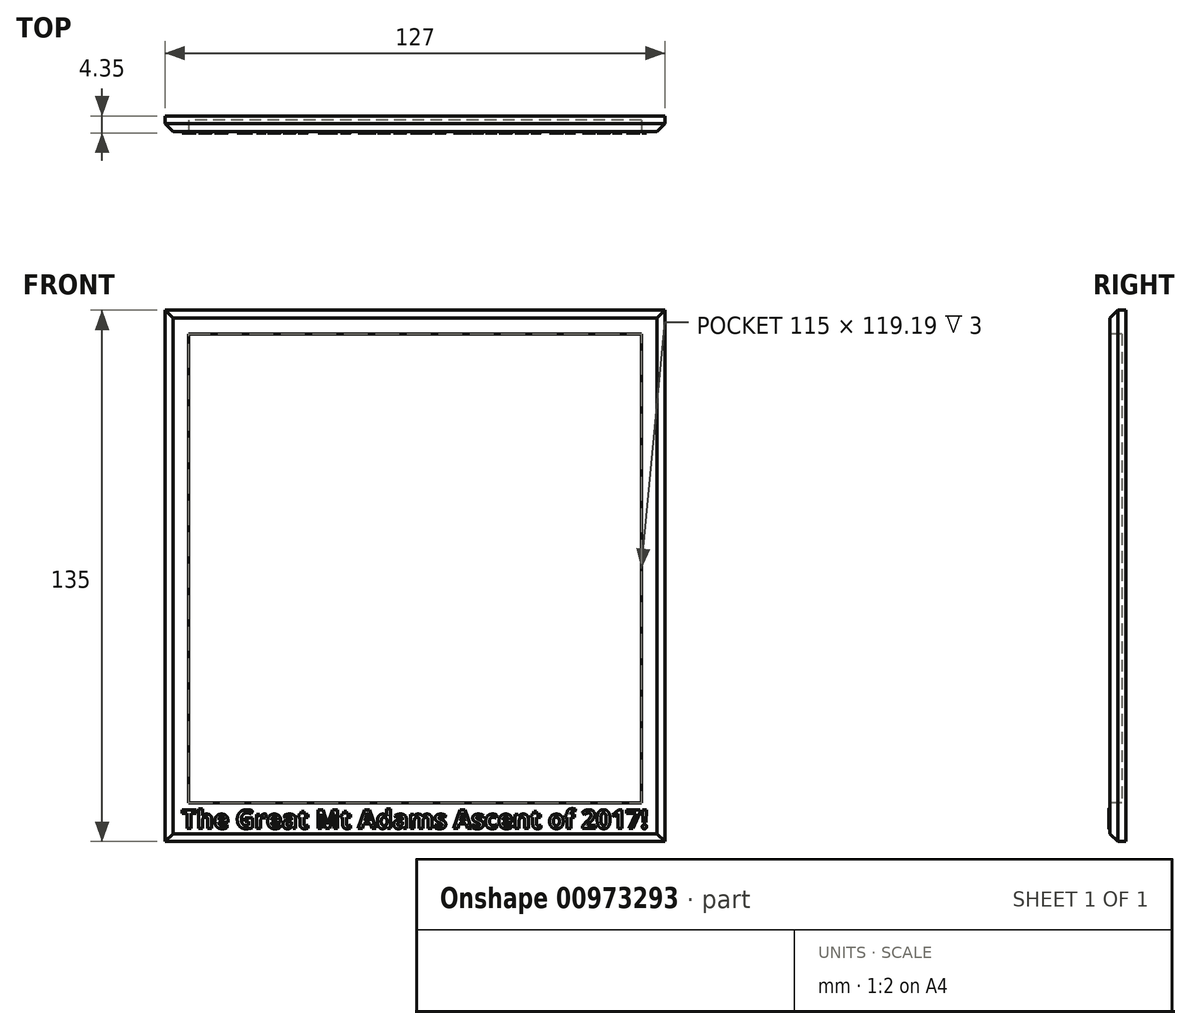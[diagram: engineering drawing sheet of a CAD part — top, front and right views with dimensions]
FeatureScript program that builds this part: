
annotation { "Feature Type Name" : "Feature", "Feature Type Description" : "" }
export const myFeature = defineFeature(function(context is Context, id is Id, definition is map)
    precondition{}
    {
        {
            var Q0;
            Q0=qCreatedBy(makeId("Front.planeOp"),FACE);
            var sketch = newSketch(context, id + "F0", { "sketchPlane" : qUnion([Q0])});
            skLineSegment(sketch, "E0.bottom", {"start": v(63.5, 67.5) * mm, "end": v(-63.5, 67.5) * mm});
            skLineSegment(sketch, "E0.top", {"start": v(63.5, -67.5) * mm, "end": v(-63.5, -67.5) * mm});
            skLineSegment(sketch, "E0.left", {"start": v(63.5, 67.5) * mm, "end": v(63.5, -67.5) * mm});
            skLineSegment(sketch, "E0.right", {"start": v(-63.5, 67.5) * mm, "end": v(-63.5, -67.5) * mm});
            skPoint(sketch, "E0.middle", {"position": v(0, 0) * mm});
            skLineSegment(sketch, "E1", {"start": v(0, 0) * mm, "end": v(0, -102.65) * mm, "construction": true});
            skLineSegment(sketch, "E2.0", {"start": v(-57.5, 61.5) * mm, "end": v(-57.5, -57.7) * mm});
            skLineSegment(sketch, "E2.1", {"start": v(57.5, 61.5) * mm, "end": v(-57.5, 61.5) * mm});
            skLineSegment(sketch, "E2.2", {"start": v(57.5, 61.5) * mm, "end": v(57.5, -57.7) * mm});
            skLineSegment(sketch, "E2.3", {"start": v(57.5, -57.7) * mm, "end": v(-57.5, -57.7) * mm});
            skText(sketch, "E3", { "text": "The Great Mt Adams Ascent of 2017!", "fontName": "OpenSans-Bold.ttf"});
            const initialGuessF0  = {"E3": [-0.05935, -0.06419, 1, 0, 0.00476]};
            skSetInitialGuess(sketch, initialGuessF0);
            skSolve(sketch);
        }
        {
            var Q0;
            Q0=makeQuery(id+"F0.imprint","IMPRINT",FACE,{"disambiguationData":[TD([[makeQuery(id+"F0.imprint","IMPRINT",EDGE,{"derivedFrom":sQuery(id+"F0.wireOp",EDGE,"E0.bottom")}),1.0]])]});
            var Q1;
            Q1=makeQuery(id+"F0.imprint","IMPRINT",FACE,{"disambiguationData":[TD([[makeQuery(id+"F0.imprint","IMPRINT",EDGE,{"derivedFrom":sQuery(id+"F0.wireOp",EDGE,"57cbe3fd-8b2a-4c72-b58d-6c1336c5d57f.0")}),1.0]])]});
            var Q2;
            Q2=makeQuery(id+"F0.imprint","IMPRINT",FACE,{"disambiguationData":[TD([[makeQuery(id+"F0.imprint","IMPRINT",EDGE,{"derivedFrom":sQuery(id+"F0.wireOp",EDGE,"cad9eeba-05d7-4ab0-af84-fa3f3b7d5006.sketch_text.stroke-0")}),-1.0]])]});
            var Q3;
            Q3=makeQuery(id+"F0.imprint","IMPRINT",FACE,{"disambiguationData":[TD([[makeQuery(id+"F0.imprint","IMPRINT",EDGE,{"derivedFrom":sQuery(id+"F0.wireOp",EDGE,"cad9eeba-05d7-4ab0-af84-fa3f3b7d5006.sketch_text.stroke-12")}),-1.0]])]});
            var Q4;
            Q4=makeQuery(id+"F0.imprint","IMPRINT",FACE,{"disambiguationData":[TD([[makeQuery(id+"F0.imprint","IMPRINT",EDGE,{"derivedFrom":sQuery(id+"F0.wireOp",EDGE,"cad9eeba-05d7-4ab0-af84-fa3f3b7d5006.sketch_text.stroke-40")}),-1.0]])]});
            var Q5;
            Q5=makeQuery(id+"F0.imprint","IMPRINT",FACE,{"disambiguationData":[TD([[makeQuery(id+"F0.imprint","IMPRINT",EDGE,{"derivedFrom":sQuery(id+"F0.wireOp",EDGE,"cad9eeba-05d7-4ab0-af84-fa3f3b7d5006.sketch_text.stroke-68")}),-1.0]])]});
            var Q6;
            Q6=makeQuery(id+"F0.imprint","IMPRINT",FACE,{"disambiguationData":[TD([[makeQuery(id+"F0.imprint","IMPRINT",EDGE,{"derivedFrom":sQuery(id+"F0.wireOp",EDGE,"cad9eeba-05d7-4ab0-af84-fa3f3b7d5006.sketch_text.stroke-68")}),1.0]])]});
            var Q7;
            Q7=makeQuery(id+"F0.imprint","IMPRINT",FACE,{"disambiguationData":[TD([[makeQuery(id+"F0.imprint","IMPRINT",EDGE,{"derivedFrom":sQuery(id+"F0.wireOp",EDGE,"cad9eeba-05d7-4ab0-af84-fa3f3b7d5006.sketch_text.stroke-86")}),-1.0]])]});
            var Q8;
            Q8=makeQuery(id+"F0.imprint","IMPRINT",FACE,{"disambiguationData":[TD([[makeQuery(id+"F0.imprint","IMPRINT",EDGE,{"derivedFrom":sQuery(id+"F0.wireOp",EDGE,"cad9eeba-05d7-4ab0-af84-fa3f3b7d5006.sketch_text.stroke-103")}),-1.0]])]});
            var Q9;
            Q9=makeQuery(id+"F0.imprint","IMPRINT",FACE,{"disambiguationData":[TD([[makeQuery(id+"F0.imprint","IMPRINT",EDGE,{"derivedFrom":sQuery(id+"F0.wireOp",EDGE,"cad9eeba-05d7-4ab0-af84-fa3f3b7d5006.sketch_text.stroke-129")}),-1.0]])]});
            var Q10;
            Q10=makeQuery(id+"F0.imprint","IMPRINT",FACE,{"disambiguationData":[TD([[makeQuery(id+"F0.imprint","IMPRINT",EDGE,{"derivedFrom":sQuery(id+"F0.wireOp",EDGE,"cad9eeba-05d7-4ab0-af84-fa3f3b7d5006.sketch_text.stroke-129")}),1.0]])]});
            var Q11;
            Q11=makeQuery(id+"F0.imprint","IMPRINT",FACE,{"disambiguationData":[TD([[makeQuery(id+"F0.imprint","IMPRINT",EDGE,{"derivedFrom":sQuery(id+"F0.wireOp",EDGE,"cad9eeba-05d7-4ab0-af84-fa3f3b7d5006.sketch_text.stroke-148")}),-1.0]])]});
            var Q12;
            Q12=makeQuery(id+"F0.imprint","IMPRINT",FACE,{"disambiguationData":[TD([[makeQuery(id+"F0.imprint","IMPRINT",EDGE,{"derivedFrom":sQuery(id+"F0.wireOp",EDGE,"cad9eeba-05d7-4ab0-af84-fa3f3b7d5006.sketch_text.stroke-148")}),1.0]])]});
            var Q13;
            Q13=makeQuery(id+"F0.imprint","IMPRINT",FACE,{"disambiguationData":[TD([[makeQuery(id+"F0.imprint","IMPRINT",EDGE,{"derivedFrom":sQuery(id+"F0.wireOp",EDGE,"cad9eeba-05d7-4ab0-af84-fa3f3b7d5006.sketch_text.stroke-166")}),-1.0]])]});
            var Q14;
            Q14=makeQuery(id+"F0.imprint","IMPRINT",FACE,{"disambiguationData":[TD([[makeQuery(id+"F0.imprint","IMPRINT",EDGE,{"derivedFrom":sQuery(id+"F0.wireOp",EDGE,"cad9eeba-05d7-4ab0-af84-fa3f3b7d5006.sketch_text.stroke-183")}),-1.0]])]});
            var Q15;
            Q15=makeQuery(id+"F0.imprint","IMPRINT",FACE,{"disambiguationData":[TD([[makeQuery(id+"F0.imprint","IMPRINT",EDGE,{"derivedFrom":sQuery(id+"F0.wireOp",EDGE,"cad9eeba-05d7-4ab0-af84-fa3f3b7d5006.sketch_text.stroke-201")}),-1.0]])]});
            var Q16;
            Q16=makeQuery(id+"F0.imprint","IMPRINT",FACE,{"disambiguationData":[TD([[makeQuery(id+"F0.imprint","IMPRINT",EDGE,{"derivedFrom":sQuery(id+"F0.wireOp",EDGE,"cad9eeba-05d7-4ab0-af84-fa3f3b7d5006.sketch_text.stroke-201")}),1.0]])]});
            var Q17;
            Q17=makeQuery(id+"F0.imprint","IMPRINT",FACE,{"disambiguationData":[TD([[makeQuery(id+"F0.imprint","IMPRINT",EDGE,{"derivedFrom":sQuery(id+"F0.wireOp",EDGE,"cad9eeba-05d7-4ab0-af84-fa3f3b7d5006.sketch_text.stroke-221")}),-1.0]])]});
            var Q18;
            Q18=makeQuery(id+"F0.imprint","IMPRINT",FACE,{"disambiguationData":[TD([[makeQuery(id+"F0.imprint","IMPRINT",EDGE,{"derivedFrom":sQuery(id+"F0.wireOp",EDGE,"cad9eeba-05d7-4ab0-af84-fa3f3b7d5006.sketch_text.stroke-238")}),1.0]])]});
            var Q19;
            Q19=makeQuery(id+"F0.imprint","IMPRINT",FACE,{"disambiguationData":[TD([[makeQuery(id+"F0.imprint","IMPRINT",EDGE,{"derivedFrom":sQuery(id+"F0.wireOp",EDGE,"cad9eeba-05d7-4ab0-af84-fa3f3b7d5006.sketch_text.stroke-246")}),-1.0]])]});
            var Q20;
            Q20=makeQuery(id+"F0.imprint","IMPRINT",FACE,{"disambiguationData":[TD([[makeQuery(id+"F0.imprint","IMPRINT",EDGE,{"derivedFrom":sQuery(id+"F0.wireOp",EDGE,"cad9eeba-05d7-4ab0-af84-fa3f3b7d5006.sketch_text.stroke-250")}),-1.0]])]});
            var Q21;
            Q21=makeQuery(id+"F0.imprint","IMPRINT",FACE,{"disambiguationData":[TD([[makeQuery(id+"F0.imprint","IMPRINT",EDGE,{"derivedFrom":sQuery(id+"F0.wireOp",EDGE,"cad9eeba-05d7-4ab0-af84-fa3f3b7d5006.sketch_text.stroke-260")}),-1.0]])]});
            var Q22;
            Q22=makeQuery(id+"F0.imprint","IMPRINT",FACE,{"disambiguationData":[TD([[makeQuery(id+"F0.imprint","IMPRINT",EDGE,{"derivedFrom":sQuery(id+"F0.wireOp",EDGE,"cad9eeba-05d7-4ab0-af84-fa3f3b7d5006.sketch_text.stroke-284")}),-1.0]])]});
            var Q23;
            Q23=makeQuery(id+"F0.imprint","IMPRINT",FACE,{"disambiguationData":[TD([[makeQuery(id+"F0.imprint","IMPRINT",EDGE,{"derivedFrom":sQuery(id+"F0.wireOp",EDGE,"cad9eeba-05d7-4ab0-af84-fa3f3b7d5006.sketch_text.stroke-288")}),-1.0]])]});
            var Q24;
            Q24=makeQuery(id+"F0.imprint","IMPRINT",FACE,{"disambiguationData":[TD([[makeQuery(id+"F0.imprint","IMPRINT",EDGE,{"derivedFrom":sQuery(id+"F0.wireOp",EDGE,"cad9eeba-05d7-4ab0-af84-fa3f3b7d5006.sketch_text.stroke-298")}),-1.0]])]});
            var Q25;
            Q25=makeQuery(id+"F0.imprint","IMPRINT",FACE,{"disambiguationData":[TD([[makeQuery(id+"F0.imprint","IMPRINT",EDGE,{"derivedFrom":sQuery(id+"F0.wireOp",EDGE,"4a6c8ffe-d77d-458f-8591-0fabea6c01ea")}),-1.0]])]});
            var Q26;
            Q26=makeQuery(id+"F0.imprint","IMPRINT",FACE,{"disambiguationData":[TD([[makeQuery(id+"F0.imprint","IMPRINT",EDGE,{"derivedFrom":sQuery(id+"F0.wireOp",EDGE,"958e2520-8c41-4e79-98e2-8bc29b8d698c.sketch_text.stroke-99")}),-1.0]])]});
            var Q27;
            Q27=makeQuery(id+"F0.imprint","IMPRINT",FACE,{"disambiguationData":[TD([[makeQuery(id+"F0.imprint","IMPRINT",EDGE,{"derivedFrom":sQuery(id+"F0.wireOp",EDGE,"958e2520-8c41-4e79-98e2-8bc29b8d698c.sketch_text.stroke-79")}),-1.0]])]});
            var Q28;
            Q28=makeQuery(id+"F0.imprint","IMPRINT",FACE,{"disambiguationData":[TD([[makeQuery(id+"F0.imprint","IMPRINT",EDGE,{"derivedFrom":sQuery(id+"F0.wireOp",EDGE,"958e2520-8c41-4e79-98e2-8bc29b8d698c.sketch_text.stroke-79")}),1.0]])]});
            var Q29;
            Q29=makeQuery(id+"F0.imprint","IMPRINT",FACE,{"disambiguationData":[TD([[makeQuery(id+"F0.imprint","IMPRINT",EDGE,{"derivedFrom":sQuery(id+"F0.wireOp",EDGE,"958e2520-8c41-4e79-98e2-8bc29b8d698c.sketch_text.stroke-75")}),-1.0]])]});
            var Q30;
            Q30=makeQuery(id+"F0.imprint","IMPRINT",FACE,{"disambiguationData":[TD([[makeQuery(id+"F0.imprint","IMPRINT",EDGE,{"derivedFrom":sQuery(id+"F0.wireOp",EDGE,"958e2520-8c41-4e79-98e2-8bc29b8d698c.sketch_text.stroke-70")}),-1.0]])]});
            var Q31;
            Q31=makeQuery(id+"F0.imprint","IMPRINT",FACE,{"disambiguationData":[TD([[makeQuery(id+"F0.imprint","IMPRINT",EDGE,{"derivedFrom":sQuery(id+"F0.wireOp",EDGE,"958e2520-8c41-4e79-98e2-8bc29b8d698c.sketch_text.stroke-53")}),-1.0]])]});
            var Q32;
            Q32=makeQuery(id+"F0.imprint","IMPRINT",FACE,{"disambiguationData":[TD([[makeQuery(id+"F0.imprint","IMPRINT",EDGE,{"derivedFrom":sQuery(id+"F0.wireOp",EDGE,"958e2520-8c41-4e79-98e2-8bc29b8d698c.sketch_text.stroke-44")}),-1.0]])]});
            var Q33;
            Q33=makeQuery(id+"F0.imprint","IMPRINT",FACE,{"disambiguationData":[TD([[makeQuery(id+"F0.imprint","IMPRINT",EDGE,{"derivedFrom":sQuery(id+"F0.wireOp",EDGE,"958e2520-8c41-4e79-98e2-8bc29b8d698c.sketch_text.stroke-49")}),-1.0]])]});
            var Q34;
            Q34=makeQuery(id+"F0.imprint","IMPRINT",FACE,{"disambiguationData":[TD([[makeQuery(id+"F0.imprint","IMPRINT",EDGE,{"derivedFrom":sQuery(id+"F0.wireOp",EDGE,"958e2520-8c41-4e79-98e2-8bc29b8d698c.sketch_text.stroke-19")}),-1.0]])]});
            var Q35;
            Q35=makeQuery(id+"F0.imprint","IMPRINT",FACE,{"disambiguationData":[TD([[makeQuery(id+"F0.imprint","IMPRINT",EDGE,{"derivedFrom":sQuery(id+"F0.wireOp",EDGE,"958e2520-8c41-4e79-98e2-8bc29b8d698c.sketch_text.stroke-37")}),1.0]])]});
            var Q36;
            Q36=makeQuery(id+"F0.imprint","IMPRINT",FACE,{"disambiguationData":[TD([[makeQuery(id+"F0.imprint","IMPRINT",EDGE,{"derivedFrom":sQuery(id+"F0.wireOp",EDGE,"958e2520-8c41-4e79-98e2-8bc29b8d698c.sketch_text.stroke-0")}),-1.0]])]});
            var Q37;
            Q37=makeQuery(id+"F0.imprint","IMPRINT",FACE,{"disambiguationData":[TD([[makeQuery(id+"F0.imprint","IMPRINT",EDGE,{"derivedFrom":sQuery(id+"F0.wireOp",EDGE,"958e2520-8c41-4e79-98e2-8bc29b8d698c.sketch_text.stroke-0")}),1.0]])]});
            var Q38;
            Q38=makeQuery(id+"F0.imprint","IMPRINT",FACE,{"disambiguationData":[TD([[makeQuery(id+"F0.imprint","IMPRINT",EDGE,{"derivedFrom":sQuery(id+"F0.wireOp",EDGE,"d4e9e7a6-ebb2-431a-a205-18104e3fe5df.sketch_text.stroke-0")}),-1.0]])]});
            var Q39;
            Q39=makeQuery(id+"F0.imprint","IMPRINT",FACE,{"disambiguationData":[TD([[makeQuery(id+"F0.imprint","IMPRINT",EDGE,{"derivedFrom":sQuery(id+"F0.wireOp",EDGE,"d4e9e7a6-ebb2-431a-a205-18104e3fe5df.sketch_text.stroke-12")}),-1.0]])]});
            var Q40;
            Q40=makeQuery(id+"F0.imprint","IMPRINT",FACE,{"disambiguationData":[TD([[makeQuery(id+"F0.imprint","IMPRINT",EDGE,{"derivedFrom":sQuery(id+"F0.wireOp",EDGE,"d4e9e7a6-ebb2-431a-a205-18104e3fe5df.sketch_text.stroke-16")}),-1.0]])]});
            var Q41;
            Q41=makeQuery(id+"F0.imprint","IMPRINT",FACE,{"disambiguationData":[TD([[makeQuery(id+"F0.imprint","IMPRINT",EDGE,{"derivedFrom":sQuery(id+"F0.wireOp",EDGE,"d4e9e7a6-ebb2-431a-a205-18104e3fe5df.sketch_text.stroke-16")}),1.0]])]});
            var Q42;
            Q42=makeQuery(id+"F0.imprint","IMPRINT",FACE,{"disambiguationData":[TD([[makeQuery(id+"F0.imprint","IMPRINT",EDGE,{"derivedFrom":sQuery(id+"F0.wireOp",EDGE,"d4e9e7a6-ebb2-431a-a205-18104e3fe5df.sketch_text.stroke-36")}),-1.0]])]});
            var Q43;
            Q43=makeQuery(id+"F0.imprint","IMPRINT",FACE,{"disambiguationData":[TD([[makeQuery(id+"F0.imprint","IMPRINT",EDGE,{"derivedFrom":sQuery(id+"F0.wireOp",EDGE,"d4e9e7a6-ebb2-431a-a205-18104e3fe5df.sketch_text.stroke-46")}),-1.0]])]});
            var Q44;
            Q44=makeQuery(id+"F0.imprint","IMPRINT",FACE,{"disambiguationData":[TD([[makeQuery(id+"F0.imprint","IMPRINT",EDGE,{"derivedFrom":sQuery(id+"F0.wireOp",EDGE,"8aae79f6-5270-443d-894e-4500fad8e815.sketch_text.stroke-0")}),-1.0]])]});
            var Q45;
            Q45=makeQuery(id+"F0.imprint","IMPRINT",FACE,{"disambiguationData":[TD([[makeQuery(id+"F0.imprint","IMPRINT",EDGE,{"derivedFrom":sQuery(id+"F0.wireOp",EDGE,"8aae79f6-5270-443d-894e-4500fad8e815.sketch_text.stroke-10")}),-1.0]])]});
            var Q46;
            Q46=makeQuery(id+"F0.imprint","IMPRINT",FACE,{"disambiguationData":[TD([[makeQuery(id+"F0.imprint","IMPRINT",EDGE,{"derivedFrom":sQuery(id+"F0.wireOp",EDGE,"8aae79f6-5270-443d-894e-4500fad8e815.sketch_text.stroke-21")}),1.0]])]});
            var Q47;
            Q47=makeQuery(id+"F0.imprint","IMPRINT",FACE,{"disambiguationData":[TD([[makeQuery(id+"F0.imprint","IMPRINT",EDGE,{"derivedFrom":sQuery(id+"F0.wireOp",EDGE,"8aae79f6-5270-443d-894e-4500fad8e815.sketch_text.stroke-28")}),-1.0]])]});
            var Q48;
            Q48=makeQuery(id+"F0.imprint","IMPRINT",FACE,{"disambiguationData":[TD([[makeQuery(id+"F0.imprint","IMPRINT",EDGE,{"derivedFrom":sQuery(id+"F0.wireOp",EDGE,"8aae79f6-5270-443d-894e-4500fad8e815.sketch_text.stroke-33")}),-1.0]])]});
            var Q49;
            Q49=makeQuery(id+"F0.imprint","IMPRINT",FACE,{"disambiguationData":[TD([[makeQuery(id+"F0.imprint","IMPRINT",EDGE,{"derivedFrom":sQuery(id+"F0.wireOp",EDGE,"8aae79f6-5270-443d-894e-4500fad8e815.sketch_text.stroke-44")}),1.0]])]});
            var Q50;
            Q50=makeQuery(id+"F0.imprint","IMPRINT",FACE,{"disambiguationData":[TD([[makeQuery(id+"F0.imprint","IMPRINT",EDGE,{"derivedFrom":sQuery(id+"F0.wireOp",EDGE,"8aae79f6-5270-443d-894e-4500fad8e815.sketch_text.stroke-51")}),-1.0]])]});
            var Q51;
            Q51=makeQuery(id+"F0.imprint","IMPRINT",FACE,{"disambiguationData":[TD([[makeQuery(id+"F0.imprint","IMPRINT",EDGE,{"derivedFrom":sQuery(id+"F0.wireOp",EDGE,"8aae79f6-5270-443d-894e-4500fad8e815.sketch_text.stroke-61")}),-1.0]])]});
            var Q52;
            Q52=makeQuery(id+"F0.imprint","IMPRINT",FACE,{"disambiguationData":[TD([[makeQuery(id+"F0.imprint","IMPRINT",EDGE,{"derivedFrom":sQuery(id+"F0.wireOp",EDGE,"8aae79f6-5270-443d-894e-4500fad8e815.sketch_text.stroke-69")}),1.0]])]});
            var Q53;
            Q53=makeQuery(id+"F0.imprint","IMPRINT",FACE,{"disambiguationData":[TD([[makeQuery(id+"F0.imprint","IMPRINT",EDGE,{"derivedFrom":sQuery(id+"F0.wireOp",EDGE,"8aae79f6-5270-443d-894e-4500fad8e815.sketch_text.stroke-77")}),-1.0]])]});
            var Q54;
            Q54=makeQuery(id+"F0.imprint","IMPRINT",FACE,{"disambiguationData":[TD([[makeQuery(id+"F0.imprint","IMPRINT",EDGE,{"derivedFrom":sQuery(id+"F0.wireOp",EDGE,"E2.0")}),1.0]])]});
            var Q55;
            Q55=makeQuery(id+"F0.imprint","IMPRINT",FACE,{"disambiguationData":[TD([[makeQuery(id+"F0.imprint","IMPRINT",EDGE,{"derivedFrom":sQuery(id+"F0.wireOp",EDGE,"E3.sketch_text.stroke-0")}),-1.0]])]});
            var Q56;
            Q56=makeQuery(id+"F0.imprint","IMPRINT",FACE,{"disambiguationData":[TD([[makeQuery(id+"F0.imprint","IMPRINT",EDGE,{"derivedFrom":sQuery(id+"F0.wireOp",EDGE,"E3.sketch_text.stroke-8")}),-1.0]])]});
            var Q57;
            Q57=makeQuery(id+"F0.imprint","IMPRINT",FACE,{"disambiguationData":[TD([[makeQuery(id+"F0.imprint","IMPRINT",EDGE,{"derivedFrom":sQuery(id+"F0.wireOp",EDGE,"E3.sketch_text.stroke-25")}),-1.0]])]});
            var Q58;
            Q58=makeQuery(id+"F0.imprint","IMPRINT",FACE,{"disambiguationData":[TD([[makeQuery(id+"F0.imprint","IMPRINT",EDGE,{"derivedFrom":sQuery(id+"F0.wireOp",EDGE,"E3.sketch_text.stroke-45")}),-1.0]])]});
            var Q59;
            Q59=makeQuery(id+"F0.imprint","IMPRINT",FACE,{"disambiguationData":[TD([[makeQuery(id+"F0.imprint","IMPRINT",EDGE,{"derivedFrom":sQuery(id+"F0.wireOp",EDGE,"E3.sketch_text.stroke-64")}),-1.0]])]});
            var Q60;
            Q60=makeQuery(id+"F0.imprint","IMPRINT",FACE,{"disambiguationData":[TD([[makeQuery(id+"F0.imprint","IMPRINT",EDGE,{"derivedFrom":sQuery(id+"F0.wireOp",EDGE,"E3.sketch_text.stroke-25")}),1.0]])]});
            var Q61;
            Q61=makeQuery(id+"F0.imprint","IMPRINT",FACE,{"disambiguationData":[TD([[makeQuery(id+"F0.imprint","IMPRINT",EDGE,{"derivedFrom":sQuery(id+"F0.wireOp",EDGE,"E3.sketch_text.stroke-77")}),-1.0]])]});
            var Q62;
            Q62=makeQuery(id+"F0.imprint","IMPRINT",FACE,{"disambiguationData":[TD([[makeQuery(id+"F0.imprint","IMPRINT",EDGE,{"derivedFrom":sQuery(id+"F0.wireOp",EDGE,"E3.sketch_text.stroke-77")}),1.0]])]});
            var Q63;
            Q63=makeQuery(id+"F0.imprint","IMPRINT",FACE,{"disambiguationData":[TD([[makeQuery(id+"F0.imprint","IMPRINT",EDGE,{"derivedFrom":sQuery(id+"F0.wireOp",EDGE,"E3.sketch_text.stroke-115")}),1.0]])]});
            var Q64;
            Q64=makeQuery(id+"F0.imprint","IMPRINT",FACE,{"disambiguationData":[TD([[makeQuery(id+"F0.imprint","IMPRINT",EDGE,{"derivedFrom":sQuery(id+"F0.wireOp",EDGE,"E3.sketch_text.stroke-97")}),-1.0]])]});
            var Q65;
            Q65=makeQuery(id+"F0.imprint","IMPRINT",FACE,{"disambiguationData":[TD([[makeQuery(id+"F0.imprint","IMPRINT",EDGE,{"derivedFrom":sQuery(id+"F0.wireOp",EDGE,"E3.sketch_text.stroke-122")}),-1.0]])]});
            var Q66;
            Q66=makeQuery(id+"F0.imprint","IMPRINT",FACE,{"disambiguationData":[TD([[makeQuery(id+"F0.imprint","IMPRINT",EDGE,{"derivedFrom":sQuery(id+"F0.wireOp",EDGE,"E3.sketch_text.stroke-140")}),-1.0]])]});
            var Q67;
            Q67=makeQuery(id+"F0.imprint","IMPRINT",FACE,{"disambiguationData":[TD([[makeQuery(id+"F0.imprint","IMPRINT",EDGE,{"derivedFrom":sQuery(id+"F0.wireOp",EDGE,"E3.sketch_text.stroke-159")}),-1.0]])]});
            var Q68;
            Q68=makeQuery(id+"F0.imprint","IMPRINT",FACE,{"disambiguationData":[TD([[makeQuery(id+"F0.imprint","IMPRINT",EDGE,{"derivedFrom":sQuery(id+"F0.wireOp",EDGE,"E3.sketch_text.stroke-177")}),-1.0]])]});
            var Q69;
            Q69=makeQuery(id+"F0.imprint","IMPRINT",FACE,{"disambiguationData":[TD([[makeQuery(id+"F0.imprint","IMPRINT",EDGE,{"derivedFrom":sQuery(id+"F0.wireOp",EDGE,"E3.sketch_text.stroke-185")}),1.0]])]});
            var Q70;
            Q70=makeQuery(id+"F0.imprint","IMPRINT",FACE,{"disambiguationData":[TD([[makeQuery(id+"F0.imprint","IMPRINT",EDGE,{"derivedFrom":sQuery(id+"F0.wireOp",EDGE,"E3.sketch_text.stroke-189")}),-1.0]])]});
            var Q71;
            Q71=makeQuery(id+"F0.imprint","IMPRINT",FACE,{"disambiguationData":[TD([[makeQuery(id+"F0.imprint","IMPRINT",EDGE,{"derivedFrom":sQuery(id+"F0.wireOp",EDGE,"E3.sketch_text.stroke-203")}),1.0]])]});
            var Q72;
            Q72=makeQuery(id+"F0.imprint","IMPRINT",FACE,{"disambiguationData":[TD([[makeQuery(id+"F0.imprint","IMPRINT",EDGE,{"derivedFrom":sQuery(id+"F0.wireOp",EDGE,"E3.sketch_text.stroke-212")}),-1.0]])]});
            var Q73;
            Q73=makeQuery(id+"F0.imprint","IMPRINT",FACE,{"disambiguationData":[TD([[makeQuery(id+"F0.imprint","IMPRINT",EDGE,{"derivedFrom":sQuery(id+"F0.wireOp",EDGE,"E3.sketch_text.stroke-230")}),1.0]])]});
            var Q74;
            Q74=makeQuery(id+"F0.imprint","IMPRINT",FACE,{"disambiguationData":[TD([[makeQuery(id+"F0.imprint","IMPRINT",EDGE,{"derivedFrom":sQuery(id+"F0.wireOp",EDGE,"E3.sketch_text.stroke-237")}),-1.0]])]});
            var Q75;
            Q75=makeQuery(id+"F0.imprint","IMPRINT",FACE,{"disambiguationData":[TD([[makeQuery(id+"F0.imprint","IMPRINT",EDGE,{"derivedFrom":sQuery(id+"F0.wireOp",EDGE,"E3.sketch_text.stroke-265")}),-1.0]])]});
            var Q76;
            Q76=makeQuery(id+"F0.imprint","IMPRINT",FACE,{"disambiguationData":[TD([[makeQuery(id+"F0.imprint","IMPRINT",EDGE,{"derivedFrom":sQuery(id+"F0.wireOp",EDGE,"E3.sketch_text.stroke-291")}),-1.0]])]});
            var Q77;
            Q77=makeQuery(id+"F0.imprint","IMPRINT",FACE,{"disambiguationData":[TD([[makeQuery(id+"F0.imprint","IMPRINT",EDGE,{"derivedFrom":sQuery(id+"F0.wireOp",EDGE,"E3.sketch_text.stroke-299")}),1.0]])]});
            var Q78;
            Q78=makeQuery(id+"F0.imprint","IMPRINT",FACE,{"disambiguationData":[TD([[makeQuery(id+"F0.imprint","IMPRINT",EDGE,{"derivedFrom":sQuery(id+"F0.wireOp",EDGE,"E3.sketch_text.stroke-303")}),-1.0]])]});
            var Q79;
            Q79=makeQuery(id+"F0.imprint","IMPRINT",FACE,{"disambiguationData":[TD([[makeQuery(id+"F0.imprint","IMPRINT",EDGE,{"derivedFrom":sQuery(id+"F0.wireOp",EDGE,"E3.sketch_text.stroke-329")}),-1.0]])]});
            var Q80;
            Q80=makeQuery(id+"F0.imprint","IMPRINT",FACE,{"disambiguationData":[TD([[makeQuery(id+"F0.imprint","IMPRINT",EDGE,{"derivedFrom":sQuery(id+"F0.wireOp",EDGE,"E3.sketch_text.stroke-343")}),-1.0]])]});
            var Q81;
            Q81=makeQuery(id+"F0.imprint","IMPRINT",FACE,{"disambiguationData":[TD([[makeQuery(id+"F0.imprint","IMPRINT",EDGE,{"derivedFrom":sQuery(id+"F0.wireOp",EDGE,"E3.sketch_text.stroke-343")}),1.0]])]});
            var Q82;
            Q82=makeQuery(id+"F0.imprint","IMPRINT",FACE,{"disambiguationData":[TD([[makeQuery(id+"F0.imprint","IMPRINT",EDGE,{"derivedFrom":sQuery(id+"F0.wireOp",EDGE,"E3.sketch_text.stroke-363")}),-1.0]])]});
            var Q83;
            Q83=makeQuery(id+"F0.imprint","IMPRINT",FACE,{"disambiguationData":[TD([[makeQuery(id+"F0.imprint","IMPRINT",EDGE,{"derivedFrom":sQuery(id+"F0.wireOp",EDGE,"E3.sketch_text.stroke-380")}),-1.0]])]});
            var Q84;
            Q84=makeQuery(id+"F0.imprint","IMPRINT",FACE,{"disambiguationData":[TD([[makeQuery(id+"F0.imprint","IMPRINT",EDGE,{"derivedFrom":sQuery(id+"F0.wireOp",EDGE,"E3.sketch_text.stroke-398")}),-1.0]])]});
            var Q85;
            Q85=makeQuery(id+"F0.imprint","IMPRINT",FACE,{"disambiguationData":[TD([[makeQuery(id+"F0.imprint","IMPRINT",EDGE,{"derivedFrom":sQuery(id+"F0.wireOp",EDGE,"E3.sketch_text.stroke-398")}),1.0]])]});
            var Q86;
            Q86=makeQuery(id+"F0.imprint","IMPRINT",FACE,{"disambiguationData":[TD([[makeQuery(id+"F0.imprint","IMPRINT",EDGE,{"derivedFrom":sQuery(id+"F0.wireOp",EDGE,"E3.sketch_text.stroke-416")}),-1.0]])]});
            var Q87;
            Q87=makeQuery(id+"F0.imprint","IMPRINT",FACE,{"disambiguationData":[TD([[makeQuery(id+"F0.imprint","IMPRINT",EDGE,{"derivedFrom":sQuery(id+"F0.wireOp",EDGE,"E3.sketch_text.stroke-434")}),-1.0]])]});
            var Q88;
            Q88=makeQuery(id+"F0.imprint","IMPRINT",FACE,{"disambiguationData":[TD([[makeQuery(id+"F0.imprint","IMPRINT",EDGE,{"derivedFrom":sQuery(id+"F0.wireOp",EDGE,"E3.sketch_text.stroke-458")}),-1.0]])]});
            var Q89;
            Q89=makeQuery(id+"F0.imprint","IMPRINT",FACE,{"disambiguationData":[TD([[makeQuery(id+"F0.imprint","IMPRINT",EDGE,{"derivedFrom":sQuery(id+"F0.wireOp",EDGE,"E3.sketch_text.stroke-466")}),1.0]])]});
            var Q90;
            Q90=makeQuery(id+"F0.imprint","IMPRINT",FACE,{"disambiguationData":[TD([[makeQuery(id+"F0.imprint","IMPRINT",EDGE,{"derivedFrom":sQuery(id+"F0.wireOp",EDGE,"E3.sketch_text.stroke-474")}),-1.0]])]});
            var Q91;
            Q91=makeQuery(id+"F0.imprint","IMPRINT",FACE,{"disambiguationData":[TD([[makeQuery(id+"F0.imprint","IMPRINT",EDGE,{"derivedFrom":sQuery(id+"F0.wireOp",EDGE,"E3.sketch_text.stroke-484")}),-1.0]])]});
            var Q92;
            Q92=makeQuery(id+"F0.imprint","IMPRINT",FACE,{"disambiguationData":[TD([[makeQuery(id+"F0.imprint","IMPRINT",EDGE,{"derivedFrom":sQuery(id+"F0.wireOp",EDGE,"E3.sketch_text.stroke-491")}),-1.0]])]});
            var Q93;
            Q93=makeQuery(id+"F0.imprint","IMPRINT",FACE,{"disambiguationData":[TD([[makeQuery(id+"F0.imprint","IMPRINT",EDGE,{"derivedFrom":sQuery(id+"F0.wireOp",EDGE,"E3.sketch_text.stroke-495")}),-1.0]])]});
            extrude(context, id + "F1", {"entities" : qUnion([Q0, Q1, Q2, Q3, Q4, Q5, Q6, Q7, Q8, Q9, Q10, Q11, Q12, Q13, Q14, Q15, Q16, Q17, Q18, Q19, Q20, Q21, Q22, Q23, Q24, Q25, Q26, Q27, Q28, Q29, Q30, Q31, Q32, Q33, Q34, Q35, Q36, Q37, Q38, Q39, Q40, Q41, Q42, Q43, Q44, Q45, Q46, Q47, Q48, Q49, Q50, Q51, Q52, Q53, Q54, Q55, Q56, Q57, Q58, Q59, Q60, Q61, Q62, Q63, Q64, Q65, Q66, Q67, Q68, Q69, Q70, Q71, Q72, Q73, Q74, Q75, Q76, Q77, Q78, Q79, Q80, Q81, Q82, Q83, Q84, Q85, Q86, Q87, Q88, Q89, Q90, Q91, Q92, Q93]), "oppositeDirection" : true, "depth" : 4 * mm, "offsetDistance" : 25 * mm});
        }
        {
            var Q0;
            Q0=makeQuery(id+"F1.opExtrude","CAP_EDGE",EDGE,{"disambiguationData":[OSD([sQuery(id+"F0.wireOp",EDGE,"E0.left")])],"isStart":true});
            var Q1;
            Q1=makeQuery(id+"F1.opExtrude","CAP_EDGE",EDGE,{"disambiguationData":[OSD([sQuery(id+"F0.wireOp",EDGE,"E0.top")])],"isStart":true});
            var Q2;
            Q2=makeQuery(id+"F1.opExtrude","CAP_EDGE",EDGE,{"disambiguationData":[OSD([sQuery(id+"F0.wireOp",EDGE,"E0.right")])],"isStart":true});
            var Q3;
            Q3=makeQuery(id+"F1.opExtrude","CAP_EDGE",EDGE,{"disambiguationData":[OSD([sQuery(id+"F0.wireOp",EDGE,"E0.bottom")])],"isStart":true});
            var Q4;
            Q4=makeQuery(id+"FPqrdFUhes9Rrdt_1.boolean.opBoolean","COPY",EDGE,{"derivedFrom":makeQuery(id+"FPqrdFUhes9Rrdt_1.opExtrude","CAP_EDGE",EDGE,{"disambiguationData":[OSD([sQuery(id+"F0.wireOp",EDGE,"57cbe3fd-8b2a-4c72-b58d-6c1336c5d57f.0")])],"isStart":true})});
            var Q5;
            Q5=makeQuery(id+"FPqrdFUhes9Rrdt_1.boolean.opBoolean","COPY",EDGE,{"derivedFrom":makeQuery(id+"FPqrdFUhes9Rrdt_1.opExtrude","CAP_EDGE",EDGE,{"disambiguationData":[OSD([sQuery(id+"F0.wireOp",EDGE,"57cbe3fd-8b2a-4c72-b58d-6c1336c5d57f.3")])],"isStart":true})});
            var Q6;
            Q6=makeQuery(id+"FPqrdFUhes9Rrdt_1.boolean.opBoolean","COPY",EDGE,{"derivedFrom":makeQuery(id+"FPqrdFUhes9Rrdt_1.opExtrude","CAP_EDGE",EDGE,{"disambiguationData":[OSD([sQuery(id+"F0.wireOp",EDGE,"57cbe3fd-8b2a-4c72-b58d-6c1336c5d57f.1")])],"isStart":true})});
            var Q7;
            Q7=makeQuery(id+"FPqrdFUhes9Rrdt_1.boolean.opBoolean","COPY",EDGE,{"derivedFrom":makeQuery(id+"FPqrdFUhes9Rrdt_1.opExtrude","CAP_EDGE",EDGE,{"disambiguationData":[OSD([sQuery(id+"F0.wireOp",EDGE,"57cbe3fd-8b2a-4c72-b58d-6c1336c5d57f.2")])],"isStart":true})});
            var Q8;
            Q8=makeQuery(id+"FPqrdFUhes9Rrdt_1.boolean.opBoolean","COPY",EDGE,{"derivedFrom":makeQuery(id+"FPqrdFUhes9Rrdt_1.opExtrude","CAP_EDGE",EDGE,{"disambiguationData":[OSD([sQuery(id+"F0.wireOp",EDGE,"047de102-cf4d-4a37-a064-cc6211fedb9c")])],"isStart":true})});
            var Q9;
            Q9=makeQuery(id+"FPqrdFUhes9Rrdt_1.boolean.opBoolean","COPY",EDGE,{"derivedFrom":makeQuery(id+"FPqrdFUhes9Rrdt_1.opExtrude","CAP_EDGE",EDGE,{"disambiguationData":[OSD([sQuery(id+"F0.wireOp",EDGE,"ea498168-eb17-4272-8319-12fdcf4cb3751.MirrorCS")])],"isStart":true})});
            var Q10;
            Q10=makeQuery(id+"FPqrdFUhes9Rrdt_1.boolean.opBoolean","COPY",EDGE,{"derivedFrom":makeQuery(id+"FPqrdFUhes9Rrdt_1.opExtrude","CAP_EDGE",EDGE,{"disambiguationData":[OSD([sQuery(id+"F0.wireOp",EDGE,"07EhUvyd-V9OH-fro4-PN5V-x3HbzXws8PvD"),sQuery(id+"F0.wireOp",EDGE,"ea498168-eb17-4272-8319-12fdcf4cb3750.MirrorCS")])],"isStart":true})});
            var Q11;
            Q11=makeQuery(id+"FPqrdFUhes9Rrdt_1.boolean.opBoolean","COPY",EDGE,{"derivedFrom":makeQuery(id+"FPqrdFUhes9Rrdt_1.opExtrude","CAP_EDGE",EDGE,{"disambiguationData":[OSD([sQuery(id+"F0.wireOp",EDGE,"ZExf2moG-sE9J-zRbT-hLlg-Fh2hhaRmwdQt")])],"isStart":true})});
            chamfer(context, id + "F2", {"entities" : qUnion([Q0, Q1, Q2, Q3, Q4, Q5, Q6, Q7, Q8, Q9, Q10, Q11]), "width" : 2 * mm, "tangentPropagation" : true});
        }
        {
            var Q0;
            Q0=makeQuery(id+"F0.imprint","IMPRINT",FACE,{"disambiguationData":[TD([[makeQuery(id+"F0.imprint","IMPRINT",EDGE,{"derivedFrom":sQuery(id+"F0.wireOp",EDGE,"E2.0")}),1.0]])]});
            extrude(context, id + "F3", {"entities" : qUnion([Q0]), "operationType" : NewBodyOperationType.REMOVE, "oppositeDirection" : true, "depth" : 3 * mm, "offsetDistance" : 25 * mm});
        }
        {
            var Q0;
            Q0=makeQuery(id+"F0.imprint","IMPRINT",FACE,{"disambiguationData":[TD([[makeQuery(id+"F0.imprint","IMPRINT",EDGE,{"derivedFrom":sQuery(id+"F0.wireOp",EDGE,"E3.sketch_text.stroke-0")}),-1.0]])]});
            var Q1;
            Q1=makeQuery(id+"F0.imprint","IMPRINT",FACE,{"disambiguationData":[TD([[makeQuery(id+"F0.imprint","IMPRINT",EDGE,{"derivedFrom":sQuery(id+"F0.wireOp",EDGE,"E3.sketch_text.stroke-8")}),-1.0]])]});
            var Q2;
            Q2=makeQuery(id+"F0.imprint","IMPRINT",FACE,{"disambiguationData":[TD([[makeQuery(id+"F0.imprint","IMPRINT",EDGE,{"derivedFrom":sQuery(id+"F0.wireOp",EDGE,"E3.sketch_text.stroke-25")}),-1.0]])]});
            var Q3;
            Q3=makeQuery(id+"F0.imprint","IMPRINT",FACE,{"disambiguationData":[TD([[makeQuery(id+"F0.imprint","IMPRINT",EDGE,{"derivedFrom":sQuery(id+"F0.wireOp",EDGE,"E3.sketch_text.stroke-45")}),-1.0]])]});
            var Q4;
            Q4=makeQuery(id+"F0.imprint","IMPRINT",FACE,{"disambiguationData":[TD([[makeQuery(id+"F0.imprint","IMPRINT",EDGE,{"derivedFrom":sQuery(id+"F0.wireOp",EDGE,"E3.sketch_text.stroke-64")}),-1.0]])]});
            var Q5;
            Q5=makeQuery(id+"F0.imprint","IMPRINT",FACE,{"disambiguationData":[TD([[makeQuery(id+"F0.imprint","IMPRINT",EDGE,{"derivedFrom":sQuery(id+"F0.wireOp",EDGE,"E3.sketch_text.stroke-77")}),-1.0]])]});
            var Q6;
            Q6=makeQuery(id+"F0.imprint","IMPRINT",FACE,{"disambiguationData":[TD([[makeQuery(id+"F0.imprint","IMPRINT",EDGE,{"derivedFrom":sQuery(id+"F0.wireOp",EDGE,"E3.sketch_text.stroke-97")}),-1.0]])]});
            var Q7;
            Q7=makeQuery(id+"F0.imprint","IMPRINT",FACE,{"disambiguationData":[TD([[makeQuery(id+"F0.imprint","IMPRINT",EDGE,{"derivedFrom":sQuery(id+"F0.wireOp",EDGE,"E3.sketch_text.stroke-122")}),-1.0]])]});
            var Q8;
            Q8=makeQuery(id+"F0.imprint","IMPRINT",FACE,{"disambiguationData":[TD([[makeQuery(id+"F0.imprint","IMPRINT",EDGE,{"derivedFrom":sQuery(id+"F0.wireOp",EDGE,"E3.sketch_text.stroke-140")}),-1.0]])]});
            var Q9;
            Q9=makeQuery(id+"F0.imprint","IMPRINT",FACE,{"disambiguationData":[TD([[makeQuery(id+"F0.imprint","IMPRINT",EDGE,{"derivedFrom":sQuery(id+"F0.wireOp",EDGE,"E3.sketch_text.stroke-159")}),-1.0]])]});
            var Q10;
            Q10=makeQuery(id+"F0.imprint","IMPRINT",FACE,{"disambiguationData":[TD([[makeQuery(id+"F0.imprint","IMPRINT",EDGE,{"derivedFrom":sQuery(id+"F0.wireOp",EDGE,"E3.sketch_text.stroke-177")}),-1.0]])]});
            var Q11;
            Q11=makeQuery(id+"F0.imprint","IMPRINT",FACE,{"disambiguationData":[TD([[makeQuery(id+"F0.imprint","IMPRINT",EDGE,{"derivedFrom":sQuery(id+"F0.wireOp",EDGE,"E3.sketch_text.stroke-189")}),-1.0]])]});
            var Q12;
            Q12=makeQuery(id+"F0.imprint","IMPRINT",FACE,{"disambiguationData":[TD([[makeQuery(id+"F0.imprint","IMPRINT",EDGE,{"derivedFrom":sQuery(id+"F0.wireOp",EDGE,"E3.sketch_text.stroke-212")}),-1.0]])]});
            var Q13;
            Q13=makeQuery(id+"F0.imprint","IMPRINT",FACE,{"disambiguationData":[TD([[makeQuery(id+"F0.imprint","IMPRINT",EDGE,{"derivedFrom":sQuery(id+"F0.wireOp",EDGE,"E3.sketch_text.stroke-237")}),-1.0]])]});
            var Q14;
            Q14=makeQuery(id+"F0.imprint","IMPRINT",FACE,{"disambiguationData":[TD([[makeQuery(id+"F0.imprint","IMPRINT",EDGE,{"derivedFrom":sQuery(id+"F0.wireOp",EDGE,"E3.sketch_text.stroke-265")}),-1.0]])]});
            var Q15;
            Q15=makeQuery(id+"F0.imprint","IMPRINT",FACE,{"disambiguationData":[TD([[makeQuery(id+"F0.imprint","IMPRINT",EDGE,{"derivedFrom":sQuery(id+"F0.wireOp",EDGE,"E3.sketch_text.stroke-291")}),-1.0]])]});
            var Q16;
            Q16=makeQuery(id+"F0.imprint","IMPRINT",FACE,{"disambiguationData":[TD([[makeQuery(id+"F0.imprint","IMPRINT",EDGE,{"derivedFrom":sQuery(id+"F0.wireOp",EDGE,"E3.sketch_text.stroke-303")}),-1.0]])]});
            var Q17;
            Q17=makeQuery(id+"F0.imprint","IMPRINT",FACE,{"disambiguationData":[TD([[makeQuery(id+"F0.imprint","IMPRINT",EDGE,{"derivedFrom":sQuery(id+"F0.wireOp",EDGE,"E3.sketch_text.stroke-329")}),-1.0]])]});
            var Q18;
            Q18=makeQuery(id+"F0.imprint","IMPRINT",FACE,{"disambiguationData":[TD([[makeQuery(id+"F0.imprint","IMPRINT",EDGE,{"derivedFrom":sQuery(id+"F0.wireOp",EDGE,"E3.sketch_text.stroke-343")}),-1.0]])]});
            var Q19;
            Q19=makeQuery(id+"F0.imprint","IMPRINT",FACE,{"disambiguationData":[TD([[makeQuery(id+"F0.imprint","IMPRINT",EDGE,{"derivedFrom":sQuery(id+"F0.wireOp",EDGE,"E3.sketch_text.stroke-363")}),-1.0]])]});
            var Q20;
            Q20=makeQuery(id+"F0.imprint","IMPRINT",FACE,{"disambiguationData":[TD([[makeQuery(id+"F0.imprint","IMPRINT",EDGE,{"derivedFrom":sQuery(id+"F0.wireOp",EDGE,"E3.sketch_text.stroke-380")}),-1.0]])]});
            var Q21;
            Q21=makeQuery(id+"F0.imprint","IMPRINT",FACE,{"disambiguationData":[TD([[makeQuery(id+"F0.imprint","IMPRINT",EDGE,{"derivedFrom":sQuery(id+"F0.wireOp",EDGE,"E3.sketch_text.stroke-398")}),-1.0]])]});
            var Q22;
            Q22=makeQuery(id+"F0.imprint","IMPRINT",FACE,{"disambiguationData":[TD([[makeQuery(id+"F0.imprint","IMPRINT",EDGE,{"derivedFrom":sQuery(id+"F0.wireOp",EDGE,"E3.sketch_text.stroke-416")}),-1.0]])]});
            var Q23;
            Q23=makeQuery(id+"F0.imprint","IMPRINT",FACE,{"disambiguationData":[TD([[makeQuery(id+"F0.imprint","IMPRINT",EDGE,{"derivedFrom":sQuery(id+"F0.wireOp",EDGE,"E3.sketch_text.stroke-434")}),-1.0]])]});
            var Q24;
            Q24=makeQuery(id+"F0.imprint","IMPRINT",FACE,{"disambiguationData":[TD([[makeQuery(id+"F0.imprint","IMPRINT",EDGE,{"derivedFrom":sQuery(id+"F0.wireOp",EDGE,"E3.sketch_text.stroke-458")}),-1.0]])]});
            var Q25;
            Q25=makeQuery(id+"F0.imprint","IMPRINT",FACE,{"disambiguationData":[TD([[makeQuery(id+"F0.imprint","IMPRINT",EDGE,{"derivedFrom":sQuery(id+"F0.wireOp",EDGE,"E3.sketch_text.stroke-474")}),-1.0]])]});
            var Q26;
            Q26=makeQuery(id+"F0.imprint","IMPRINT",FACE,{"disambiguationData":[TD([[makeQuery(id+"F0.imprint","IMPRINT",EDGE,{"derivedFrom":sQuery(id+"F0.wireOp",EDGE,"E3.sketch_text.stroke-484")}),-1.0]])]});
            var Q27;
            Q27=makeQuery(id+"F0.imprint","IMPRINT",FACE,{"disambiguationData":[TD([[makeQuery(id+"F0.imprint","IMPRINT",EDGE,{"derivedFrom":sQuery(id+"F0.wireOp",EDGE,"E3.sketch_text.stroke-491")}),-1.0]])]});
            var Q28;
            Q28=makeQuery(id+"F0.imprint","IMPRINT",FACE,{"disambiguationData":[TD([[makeQuery(id+"F0.imprint","IMPRINT",EDGE,{"derivedFrom":sQuery(id+"F0.wireOp",EDGE,"E3.sketch_text.stroke-495")}),-1.0]])]});
            extrude(context, id + "F4", {"entities" : qUnion([Q0, Q1, Q2, Q3, Q4, Q5, Q6, Q7, Q8, Q9, Q10, Q11, Q12, Q13, Q14, Q15, Q16, Q17, Q18, Q19, Q20, Q21, Q22, Q23, Q24, Q25, Q26, Q27, Q28]), "operationType" : NewBodyOperationType.ADD, "depth" : .35 * mm, "offsetDistance" : 25 * mm});
        }
    });
